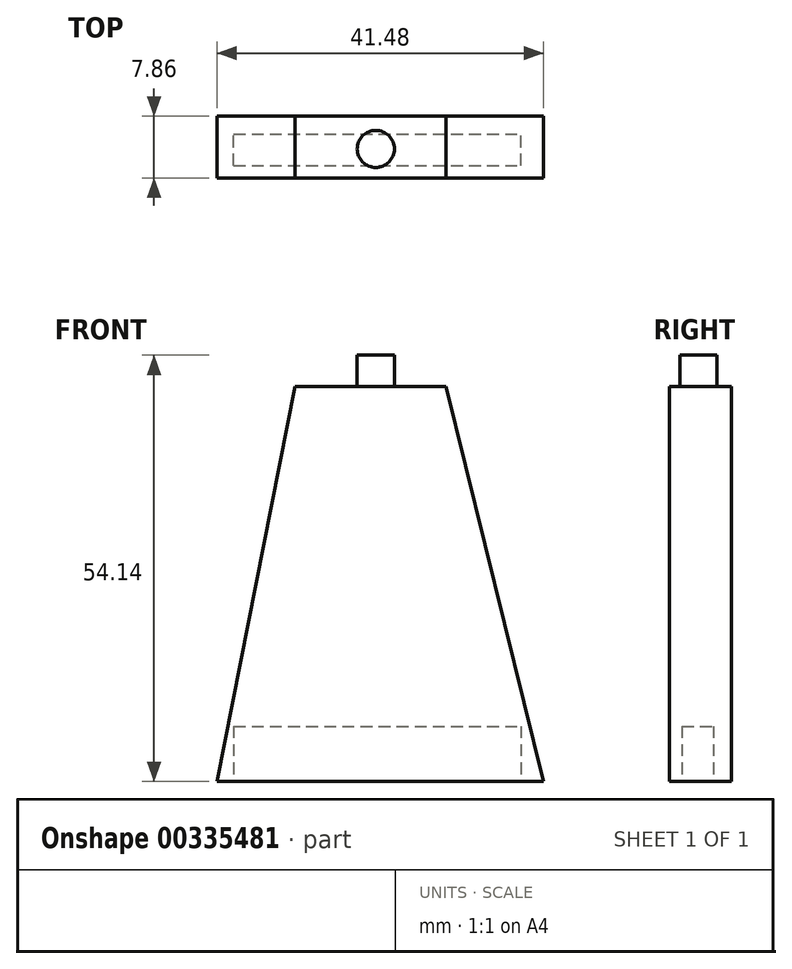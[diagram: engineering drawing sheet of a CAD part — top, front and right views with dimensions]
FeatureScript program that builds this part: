
annotation { "Feature Type Name" : "Feature", "Feature Type Description" : "" }
export const myFeature = defineFeature(function(context is Context, id is Id, definition is map)
    precondition{}
    {
        {
            var Q0;
            Q0=qCreatedBy(makeId("Front.planeOp"),FACE);
            var sketch = newSketch(context, id + "F0", { "sketchPlane" : qUnion([Q0])});
            skLineSegment(sketch, "E0.bottom", {"start": v(-21.36, 32.96) * mm, "end": v(20.12, 32.96) * mm});
            skLineSegment(sketch, "E0.top", {"start": v(-21.36, -17.18) * mm, "end": v(20.12, -17.18) * mm});
            skLineSegment(sketch, "E0.left", {"start": v(-21.36, 32.96) * mm, "end": v(-21.36, -17.18) * mm});
            skLineSegment(sketch, "E0.right", {"start": v(20.12, 32.96) * mm, "end": v(20.12, -17.18) * mm});
            skLineSegment(sketch, "E1", {"start": v(-21.36, -17.18) * mm, "end": v(-8.98, 32.96) * mm});
            skLineSegment(sketch, "E2", {"start": v(20.12, -17.18) * mm, "end": v(5.9, 32.96) * mm});
            skSolve(sketch);
        }
        {
            var Q0;
            Q0=makeQuery(id+"F0.imprint","IMPRINT",FACE,{"disambiguationData":[TD([[makeQuery(id+"F0.imprint","IMPRINT",EDGE,{"derivedFrom":sQuery(id+"F0.wireOp",EDGE,"E0.top")}),1.0]])]});
            var Q1;
            {var subQ0=sQuery(id+"F0.wireOp",EDGE,"E0.left");Q1=makeQuery(id+"F0.imprint","IMPRINT",FACE,{"disambiguationData":[TD([[makeQuery(id+"F0.imprint","IMPRINT",EDGE,{"derivedFrom":subQ0}),1.0]])]});}
            var Q2;
            {var subQ0=sQuery(id+"F0.wireOp",EDGE,"E0.right");Q2=makeQuery(id+"F0.imprint","IMPRINT",FACE,{"disambiguationData":[TD([[makeQuery(id+"F0.imprint","IMPRINT",EDGE,{"derivedFrom":subQ0}),-1.0]])]});}
            extrude(context, id + "F1", {"entities" : qUnion([Q0, Q1, Q2]), "depth" : 7.86 * mm});
        }
        {
            var Q0;
            Q0=makeQuery(id+"F1.opExtrude","CAP_FACE",FACE,{"disambiguationData":[OSD([sQuery(id+"F0.wireOp",EDGE,"E0.bottom"),sQuery(id+"F0.wireOp",EDGE,"E0.top"),sQuery(id+"F0.wireOp",EDGE,"E0.left"),sQuery(id+"F0.wireOp",EDGE,"E0.right")])],"isStart":false});
            var sketch = newSketch(context, id + "F2", { "sketchPlane" : qUnion([Q0])});
            skLineSegment(sketch, "E3", {"start": v(-21.36, -17.18) * mm, "end": v(-11.45, 32.96) * mm});
            skLineSegment(sketch, "E4", {"start": v(20.12, -17.18) * mm, "end": v(7.75, 32.96) * mm});
            skSolve(sketch);
        }
        {
            var Q0;
            {var subQ0=sQuery(id+"F2.wireOp",EDGE,"E3");Q0=makeQuery(id+"F2.imprint","IMPRINT",FACE,{"disambiguationData":[TD([[makeQuery(id+"F2.imprint","IMPRINT",EDGE,{"derivedFrom":subQ0}),1.0]])]});}
            var Q1;
            {var subQ0=sQuery(id+"F2.wireOp",EDGE,"E4");Q1=makeQuery(id+"F2.imprint","IMPRINT",FACE,{"disambiguationData":[TD([[makeQuery(id+"F2.imprint","IMPRINT",EDGE,{"derivedFrom":subQ0}),-1.0]])]});}
            extrude(context, id + "F3", {"entities" : qUnion([Q0, Q1]), "operationType" : NewBodyOperationType.REMOVE, "oppositeDirection" : true, "depth" : 25.4 * mm});
        }
        {
            var Q0;
            Q0=makeQuery(id+"F1.opExtrude","SWEPT_FACE",FACE,{"disambiguationData":[OSD([sQuery(id+"F0.wireOp",EDGE,"E0.bottom")])]});
            var sketch = newSketch(context, id + "F4", { "sketchPlane" : qUnion([Q0])});
            skCircle(sketch, "E5", {"center": v(-1.18, -4.16) * mm, "radius": 2.36 * mm});
            skSolve(sketch);
        }
        {
            var Q0;
            Q0=makeQuery(id+"F4.imprint","IMPRINT",FACE,{"disambiguationData":[TD([[makeQuery(id+"F4.imprint","IMPRINT",EDGE,{"derivedFrom":sQuery(id+"F4.wireOp",EDGE,"E5")}),1.0]])]});
            extrude(context, id + "F5", {"entities" : qUnion([Q0]), "operationType" : NewBodyOperationType.ADD, "depth" : 4 * mm});
        }
        {
            var Q0;
            Q0=makeQuery(id+"F1.opExtrude","SWEPT_FACE",FACE,{"disambiguationData":[OSD([sQuery(id+"F0.wireOp",EDGE,"E0.top")])]});
            var sketch = newSketch(context, id + "F6", { "sketchPlane" : qUnion([Q0])});
            skLineSegment(sketch, "E6.bottom", {"start": v(-19.22, 6.26) * mm, "end": v(17.26, 6.26) * mm});
            skLineSegment(sketch, "E6.top", {"start": v(-19.22, 2.27) * mm, "end": v(17.26, 2.27) * mm});
            skLineSegment(sketch, "E6.left", {"start": v(-19.22, 6.26) * mm, "end": v(-19.22, 2.27) * mm});
            skLineSegment(sketch, "E6.right", {"start": v(17.26, 6.26) * mm, "end": v(17.26, 2.27) * mm});
            skSolve(sketch);
        }
        {
            var Q0;
            Q0=makeQuery(id+"F6.imprint","IMPRINT",FACE,{"disambiguationData":[TD([[makeQuery(id+"F6.imprint","IMPRINT",EDGE,{"derivedFrom":sQuery(id+"F6.wireOp",EDGE,"E6.bottom")}),-1.0]])]});
            extrude(context, id + "F7", {"entities" : qUnion([Q0]), "operationType" : NewBodyOperationType.REMOVE, "oppositeDirection" : true, "depth" : 7 * mm});
        }
    });
